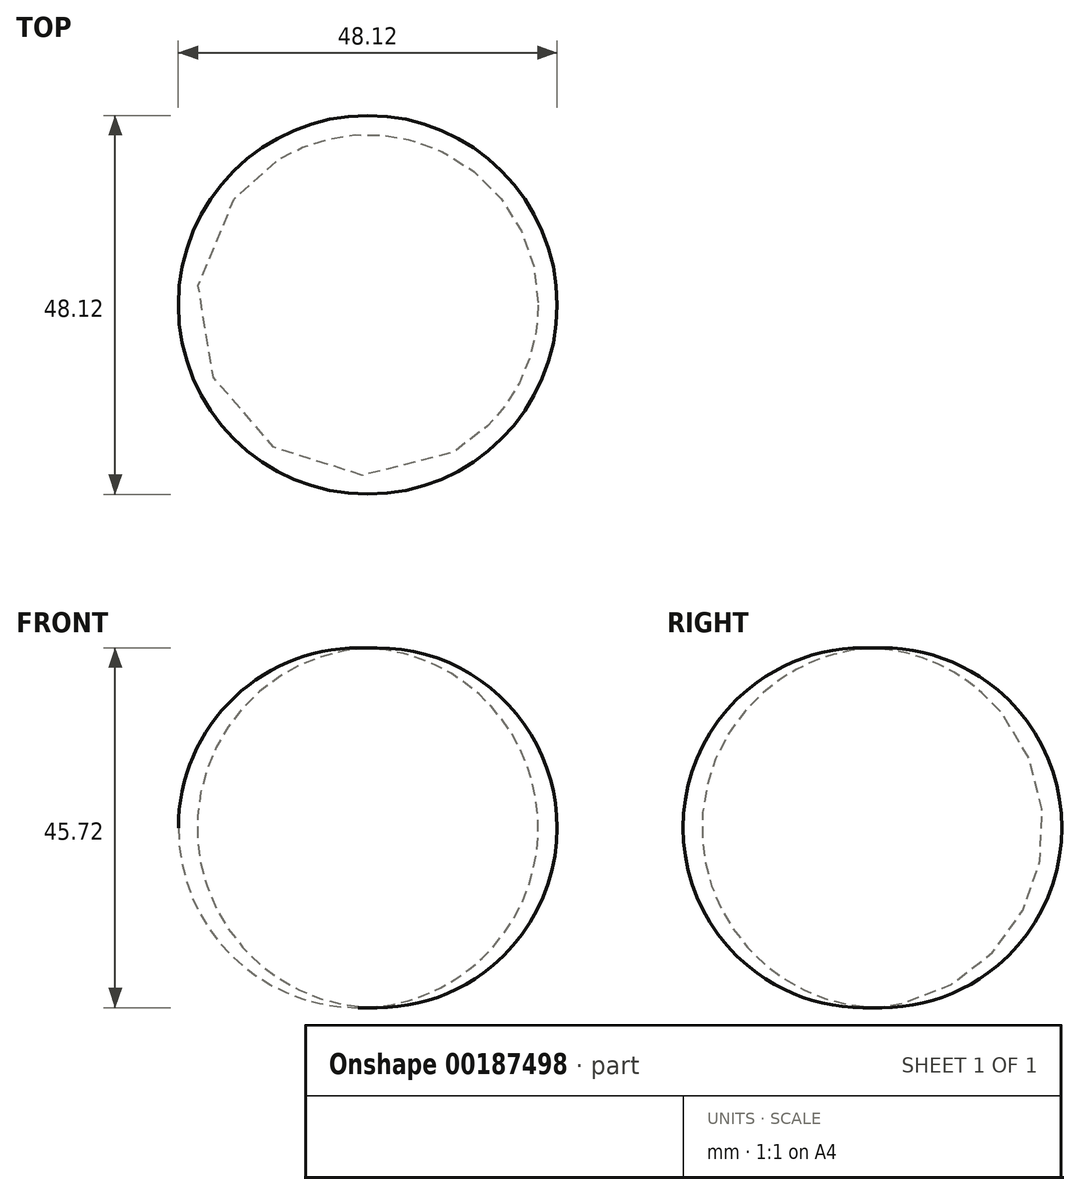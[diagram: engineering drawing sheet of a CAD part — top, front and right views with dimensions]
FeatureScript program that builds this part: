
annotation { "Feature Type Name" : "Feature", "Feature Type Description" : "" }
export const myFeature = defineFeature(function(context is Context, id is Id, definition is map)
    precondition{}
    {
        {
            var Q0;
            Q0=qCreatedBy(makeId("Front.planeOp"),FACE);
            var sketch = newSketch(context, id + "F0", { "sketchPlane" : qUnion([Q0])});
            skArc(sketch, "E0", {"start": v(0, 45.65) * mm, "mid": v(-24.06, 22.83) * mm, "end": v(0, 0) * mm});
            skLineSegment(sketch, "E1", {"start": v(0, 0) * mm, "end": v(0, 45.65) * mm});
            skSolve(sketch);
        }
        {
            var Q0;
            Q0 = qSketchRegion(id + "F0", true);
            var Q1;
            Q1=sQuery(id+"F0.wireOp",EDGE,"E1");
            revolve(context, id + "F1", {"entities" : qUnion([Q0]), "axis" : qUnion([Q1]), "revolveType" : RevolveType.FULL});
        }
    });
